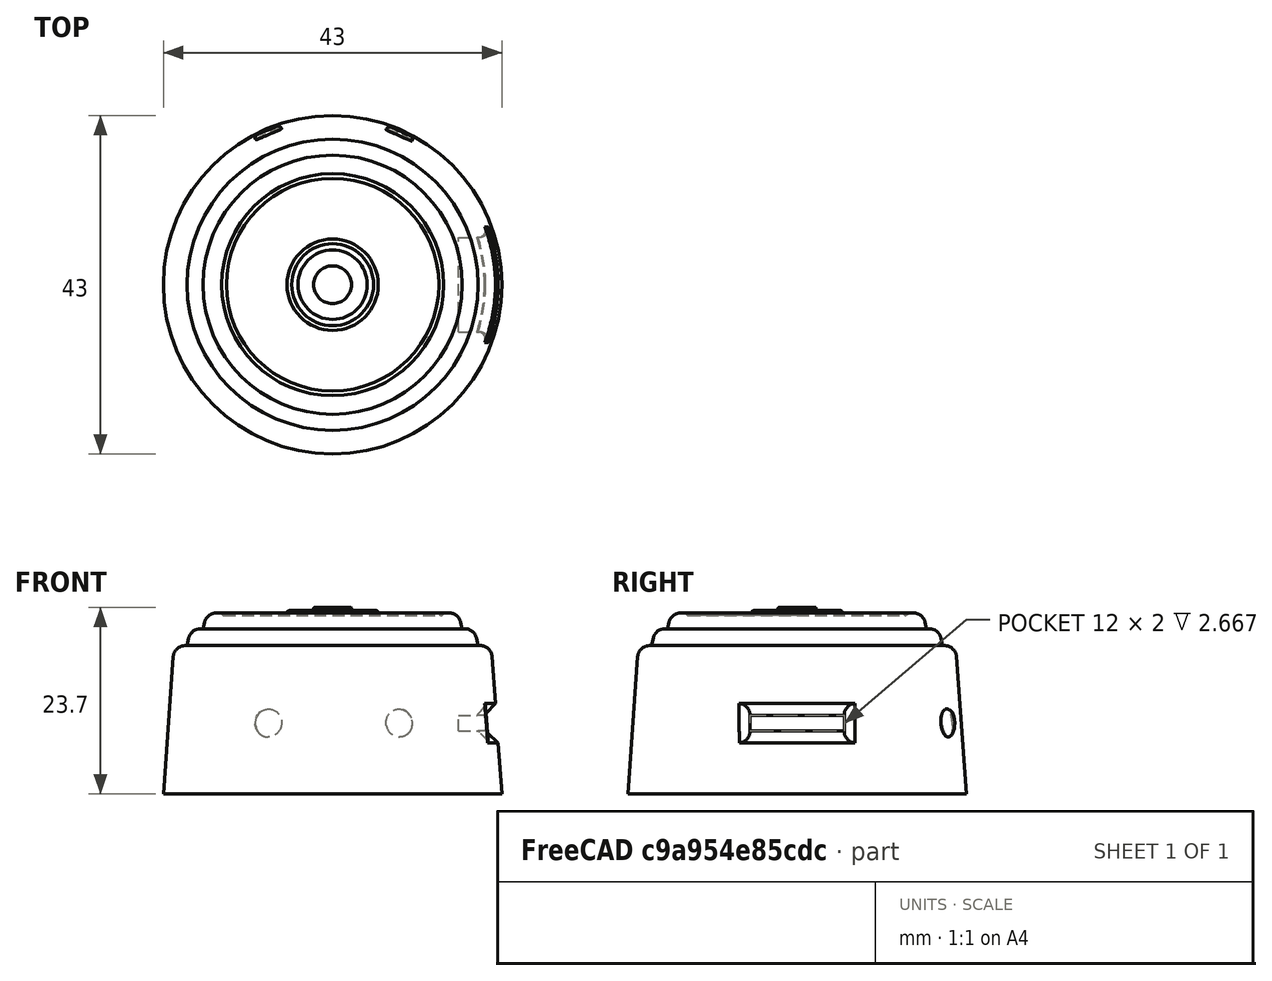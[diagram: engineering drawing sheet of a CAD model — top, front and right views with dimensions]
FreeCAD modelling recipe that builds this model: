
FCSTD DOCUMENT  (FreeCAD 0.20R29603 (Git))
Label: MicroCamara
License: All rights reserved
LicenseURL: http://en.wikipedia.org/wiki/All_rights_reserved
objects: Part::Fillet×9, Part::MultiFuse×7, Part::Cylinder×5, Part::Cone×3, Part::Torus×2, Part::Cut×2, Part::Box×1, Part::Chamfer×1
note: 30 computed .brp shape members not serialized (recipe doc carries the construction recipe); baked Part::Feature solids carry a one-line shape summary decoded from their .brp

FEATURE [Part::Cone] Cone  label="Cono"
  Angle = 360
  AttacherType = Attacher::AttachEngine3D
  Height = 18.85
  Radius1 = 21.5
  Radius2 = 20.15
FEATURE [Part::Fillet] Fillet
  Base = -> Cone
  Edges = 1 edges r=1.5: [Edge1]
FEATURE [Part::Cone] Cone001  label="Cono001"
  Angle = 360
  AttacherType = Attacher::AttachEngine3D
  Height = 2.2
  Placement = pos=(0,0,18.8) rot=(0,0,1;0rad)
  Radius1 = 18.5
  Radius2 = 18
FEATURE [Part::Fillet] Fillet001
  Base = -> Cone001
  Edges = 1 edges r=1.5: [Edge1]
FEATURE [Part::Cone] Cone002  label="Cono002"
  Angle = 360
  AttacherType = Attacher::AttachEngine3D
  Height = 2.2
  Placement = pos=(0,0,20.8) rot=(0,0,1;0rad)
  Radius1 = 16.5
  Radius2 = 16
FEATURE [Part::Fillet] Fillet002
  Base = -> Cone002
  Edges = 1 edges r=1.5: [Edge1]
FEATURE [Part::Torus] Torus  label="Toro"
  Angle1 = -180
  Angle2 = 180
  Angle3 = 360
  AttacherType = Attacher::AttachEngine3D
  Placement = pos=(0,0,23) rot=(0,0,1;0rad)
  Radius1 = 13.8
  Radius2 = 0.3
FEATURE [Part::Torus] Torus001  label="Toro001"
  Angle1 = -180
  Angle2 = 180
  Angle3 = 360
  AttacherType = Attacher::AttachEngine3D
  Placement = pos=(0,0,23) rot=(0,0,1;0rad)
  Radius1 = 5.5
  Radius2 = 0.3
FEATURE [Part::Cut] Cut
  Base = -> Fillet002
  Tool = -> Torus
FEATURE [Part::MultiFuse] Fusion
  Shapes = -> [Torus001,Cut]
FEATURE [Part::Cylinder] Cylinder  label="Cilindro"
  Angle = 360
  AttacherType = Attacher::AttachEngine3D
  FirstAngle = 0
  Height = 3
  Placement = pos=(0,0,20.2) rot=(0,0,1;0rad)
  Radius = 4.4
  SecondAngle = 0
FEATURE [Part::Fillet] Fillet003
  Base = -> Cylinder
  Edges = 1 edges r=0.1: [Edge3]
FEATURE [Part::Box] Box  label="Cubo"
  AttacherType = Attacher::AttachEngine3D
  Height = 2
  Length = 8
  Placement = pos=(16,-6,8) rot=(0,0,1;0rad)
  Width = 12
FEATURE [Part::Cut] Cut001
  Base = -> Fillet
  Tool = -> Box
FEATURE [Part::Chamfer] Chamfer
  Base = -> Cut001
  Edges = 4 edges r=1.5: [Edge3,Edge5,Edge8,Edge10]
FEATURE [Part::Fillet] Fillet004
  Base = -> Chamfer
  Edges = 3 edges r=1: [Edge4,Edge5,Edge6]
FEATURE [Part::Fillet] Fillet005
  Base = -> Fillet004
  Edges = 3 edges r=1: [Edge6,Edge7,Edge8]
FEATURE [Part::Cylinder] Cylinder001  label="Cilindro001"
  Angle = 360
  AttacherType = Attacher::AttachEngine3D
  FirstAngle = 0
  Height = 1.6
  Placement = pos=(8,18,9) rot=(-0.4783,0.736518,0.4783;1.87196rad)
  Radius = 1.8
  SecondAngle = 0
FEATURE [Part::Fillet] Fillet006
  Base = -> Cylinder001
  Edges = 1 edges r=0.5: [Edge3]
FEATURE [Part::Cylinder] Cylinder002  label="Cilindro002"
  Angle = 360
  AttacherType = Attacher::AttachEngine3D
  FirstAngle = 0
  Height = 1.6
  Placement = pos=(8,18,9) rot=(-0.4783,0.736518,0.4783;1.87196rad)
  Radius = 1.8
  SecondAngle = 0
FEATURE [Part::Fillet] Fillet007
  Base = -> Cylinder002
  Edges = 1 edges r=0.5: [Edge3]
  Placement = pos=(0,0,0) rot=(0,0,1;0.820305rad)
FEATURE [Part::MultiFuse] Fusion001
  Shapes = -> [Fillet005,Fillet006,Fillet007]
FEATURE [Part::Cylinder] Cylinder003  label="Cilindro003"
  Angle = 360
  AttacherType = Attacher::AttachEngine3D
  FirstAngle = 0
  Height = 4
  Placement = pos=(0,0,20.2) rot=(0,0,1;0rad)
  Radius = 2.4
  SecondAngle = 0
FEATURE [Part::Fillet] Fillet008
  Base = -> Cylinder003
  Edges = 1 edges r=0.1: [Edge3]
  Placement = pos=(0,0,-0.5) rot=(0,0,1;0rad)
FEATURE [Part::MultiFuse] Fusion002
  Shapes = -> [Fillet001,Fusion001]
FEATURE [Part::MultiFuse] Fusion003
  Shapes = -> [Fusion002,Fusion]
FEATURE [Part::MultiFuse] Fusion004
  Shapes = -> [Fusion003,Fillet003]
FEATURE [Part::Cylinder] Cylinder004  label="Cilindro004"
  Angle = 360
  AttacherType = Attacher::AttachEngine3D
  FirstAngle = 0
  Height = 10
  Placement = pos=(0,0,12.5) rot=(0,0,1;0rad)
  Radius = 8
  SecondAngle = 0
FEATURE [Part::MultiFuse] Fusion005
  Shapes = -> [Fusion004,Fillet008]
FEATURE [Part::MultiFuse] Fusion006  label="Camara"
  Shapes = -> [Fusion005,Cylinder004]
